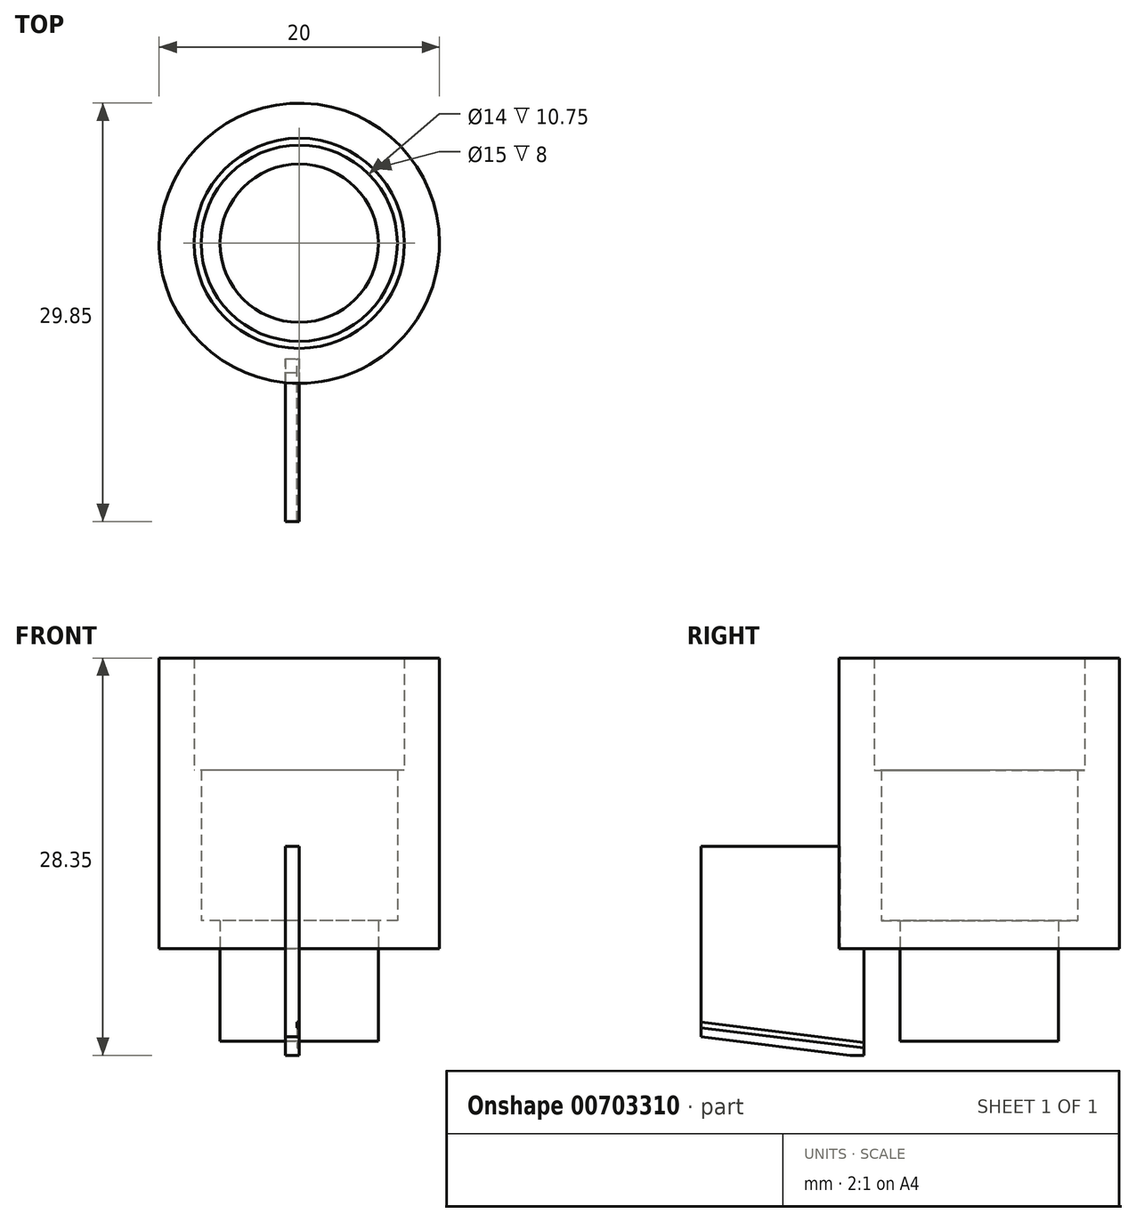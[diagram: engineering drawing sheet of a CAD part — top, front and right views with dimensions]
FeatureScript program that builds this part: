
annotation { "Feature Type Name" : "Feature", "Feature Type Description" : "" }
export const myFeature = defineFeature(function(context is Context, id is Id, definition is map)
    precondition{}
    {
        {
            var Q0;
            Q0=qCreatedBy(makeId("Top.planeOp"),FACE);
            var sketch = newSketch(context, id + "F0", { "sketchPlane" : qUnion([Q0])});
            skCircle(sketch, "E0", {"center": v(0, 0) * mm, "radius": 5.65 * mm});
            skCircle(sketch, "E1", {"center": v(0, 0) * mm, "radius": 10 * mm});
            skSolve(sketch);
        }
        {
            var Q0;
            Q0=makeQuery(id+"F0.imprint","IMPRINT",FACE,{"disambiguationData":[TD([[makeQuery(id+"F0.imprint","IMPRINT",EDGE,{"derivedFrom":sQuery(id+"F0.wireOp",EDGE,"E0")}),-1.0]])]});
            extrude(context, id + "F1", {"entities" : qUnion([Q0]), "depth" : 2 * mm, "offsetDistance" : 25 * mm});
        }
        {
            var Q0;
            Q0=makeQuery(id+"F1.opExtrude","CAP_FACE",FACE,{"disambiguationData":[OSD([sQuery(id+"F0.wireOp",EDGE,"E0"),sQuery(id+"F0.wireOp",EDGE,"E1")])],"isStart":false});
            var sketch = newSketch(context, id + "F2", { "sketchPlane" : qUnion([Q0])});
            skCircle(sketch, "E2", {"center": v(0, 0) * mm, "radius": 7 * mm});
            skCircle(sketch, "E3", {"center": v(0, 0) * mm, "radius": 10 * mm});
            skSolve(sketch);
        }
        {
            var Q0;
            Q0 = qSketchRegion(id + "F2", true);
            extrude(context, id + "F3", {"entities" : qUnion([Q0]), "operationType" : NewBodyOperationType.ADD, "depth" : 10.75 * mm, "offsetDistance" : 25 * mm});
        }
        {
            var Q0;
            Q0=makeQuery(id+"F3.opExtrude","CAP_FACE",FACE,{"disambiguationData":[OSD([sQuery(id+"F2.wireOp",EDGE,"E2"),sQuery(id+"F2.wireOp",EDGE,"E3")])],"isStart":false});
            var sketch = newSketch(context, id + "F4", { "sketchPlane" : qUnion([Q0])});
            skCircle(sketch, "E4", {"center": v(0, 0) * mm, "radius": 7.5 * mm});
            skCircle(sketch, "E5", {"center": v(0, 0) * mm, "radius": 10 * mm});
            skSolve(sketch);
        }
        {
            var Q0;
            Q0=makeQuery(id+"F4.imprint","IMPRINT",FACE,{"disambiguationData":[TD([[makeQuery(id+"F4.imprint","IMPRINT",EDGE,{"derivedFrom":sQuery(id+"F4.wireOp",EDGE,"E4")}),-1.0]])]});
            extrude(context, id + "F5", {"entities" : qUnion([Q0]), "operationType" : NewBodyOperationType.ADD, "depth" : 8 * mm, "offsetDistance" : 25 * mm});
        }
        {
            var Q0;
            Q0 = qSketchRegion(id + "F7", true);
            var Q1;
            Q1=makeQuery(id+"F0.imprint","IMPRINT",FACE,{"disambiguationData":[TD([[makeQuery(id+"F0.imprint","IMPRINT",EDGE,{"derivedFrom":sQuery(id+"F0.wireOp",EDGE,"E0")}),1.0]])]});
            extrude(context, id + "F6", {"entities" : qUnion([Q0, Q1]), "oppositeDirection" : true, "depth" : 6.6 * mm, "offsetDistance" : 25 * mm});
        }
        {
            var Q0;
            Q0=qCreatedBy(makeId("Right.planeOp"),FACE);
            var sketch = newSketch(context, id + "F7", { "sketchPlane" : qUnion([Q0])});
            skPoint(sketch, "E6", {"position": v(0, -7.6) * mm});
            skPoint(sketch, "E7", {"position": v(0, -7.9) * mm});
            skLineSegment(sketch, "E8", {"start": v(-8.23, -7.6) * mm, "end": v(-9.23, -7.6) * mm});
            skLineSegment(sketch, "E9", {"start": v(-8.23, 1.96) * mm, "end": v(-8.23, -7.6) * mm});
            skPoint(sketch, "E10", {"position": v(-5.65, -7) * mm});
            skPoint(sketch, "E11", {"position": v(-5.65, -7.2) * mm});
            skLineSegment(sketch, "E12", {"start": v(0, -7.9) * mm, "end": v(-19.85, -5.44) * mm});
            skLineSegment(sketch, "E13", {"start": v(-19.85, -5.44) * mm, "end": v(-19.85, 7.3) * mm});
            skLineSegment(sketch, "E14", {"start": v(-19.85, 7.3) * mm, "end": v(-8.23, 7.3) * mm});
            skLineSegment(sketch, "E15", {"start": v(-8.23, 1.96) * mm, "end": v(-8.23, 7.3) * mm});
            skLineSegment(sketch, "E16", {"start": v(-19.85, -5.44) * mm, "end": v(-19.85, -6.28) * mm});
            skPoint(sketch, "E17.orphan", {"position": v(-8.23, -7.88) * mm});
            skLineSegment(sketch, "E18", {"start": v(-19.85, -5.24) * mm, "end": v(-8.23, -6.68) * mm});
            skLineSegment(sketch, "E19", {"start": v(-19.85, -5.64) * mm, "end": v(-8.23, -7.08) * mm});
            skLineSegment(sketch, "E20", {"start": v(-9.23, -7.6) * mm, "end": v(-19.85, -6.28) * mm});
            skLineSegment(sketch, "E21", {"start": v(0, -7.9) * mm, "end": v(-5.87, -7.9) * mm});
            skSolve(sketch);
        }
        {
            var Q0;
            {var subQ1=sQuery(id+"F7.wireOp",EDGE,"E14");Q0=makeQuery(id+"F7.imprint","IMPRINT",FACE,{"disambiguationData":[TD([[makeQuery(id+"F7.imprint","IMPRINT",EDGE,{"derivedFrom":subQ1}),-1.0]])]});}
            var Q1;
            {var subQ3=sQuery(id+"F7.wireOp",EDGE,"E8");Q1=makeQuery(id+"F7.imprint","IMPRINT",FACE,{"disambiguationData":[TD([[makeQuery(id+"F7.imprint","IMPRINT",EDGE,{"derivedFrom":subQ3}),-1.0]])]});}
            var Q2;
            {var subQ0=sQuery(id+"F7.wireOp",EDGE,"E18");Q2=makeQuery(id+"F7.imprint","IMPRINT",FACE,{"disambiguationData":[TD([[makeQuery(id+"F7.imprint","IMPRINT",EDGE,{"derivedFrom":subQ0}),-1.0]])]});}
            var Q3;
            {var subQ0=sQuery(id+"F7.wireOp",EDGE,"E19");Q3=makeQuery(id+"F7.imprint","IMPRINT",FACE,{"disambiguationData":[TD([[makeQuery(id+"F7.imprint","IMPRINT",EDGE,{"derivedFrom":subQ0}),1.0]])]});}
            extrude(context, id + "F8", {"entities" : qUnion([Q0, Q1, Q2, Q3]), "operationType" : NewBodyOperationType.ADD, "oppositeDirection" : true, "depth" : 1 * mm, "offsetDistance" : 25 * mm});
        }
        {
            var Q0;
            {var subQ0=sQuery(id+"F7.wireOp",EDGE,"E18");Q0=makeQuery(id+"F7.imprint","IMPRINT",FACE,{"disambiguationData":[TD([[makeQuery(id+"F7.imprint","IMPRINT",EDGE,{"derivedFrom":subQ0}),-1.0]])]});}
            var Q1;
            {var subQ0=sQuery(id+"F7.wireOp",EDGE,"E19");Q1=makeQuery(id+"F7.imprint","IMPRINT",FACE,{"disambiguationData":[TD([[makeQuery(id+"F7.imprint","IMPRINT",EDGE,{"derivedFrom":subQ0}),1.0]])]});}
            extrude(context, id + "F9", {"entities" : qUnion([Q0, Q1]), "operationType" : NewBodyOperationType.REMOVE, "oppositeDirection" : true, "depth" : 0.15 * mm, "offsetDistance" : 25 * mm});
        }
    });
